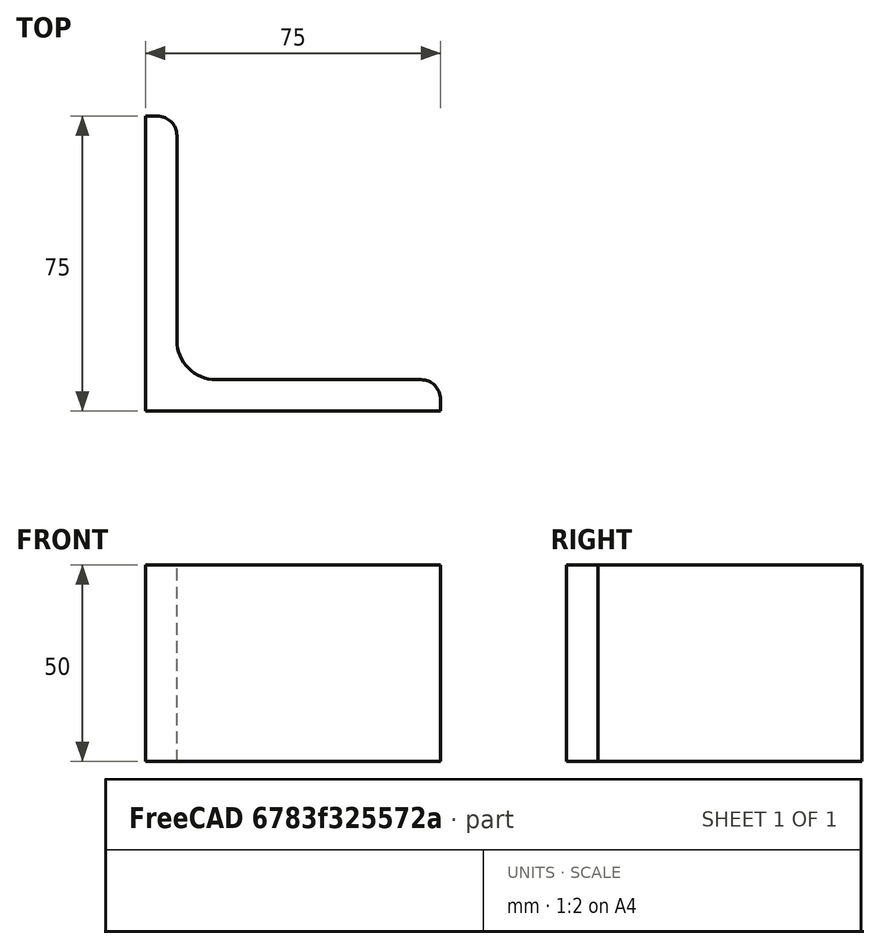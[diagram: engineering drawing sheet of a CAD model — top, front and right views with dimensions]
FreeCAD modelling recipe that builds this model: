
FCSTD DOCUMENT  (FreeCAD 0.15R4671 (Git))
Label: Angle Bar L75x75x8 EN10056 S235JR
License: All rights reserved
LicenseURL: http://en.wikipedia.org/wiki/All_rights_reserved
objects: Sketcher::SketchObject×1, Part::Extrusion×1
note: 2 computed .brp shape members not serialized (recipe doc carries the construction recipe); baked Part::Feature solids carry a one-line shape summary decoded from their .brp

FEATURE [Sketcher::SketchObject] Sketch
  sketch-geometry (9):
    g0: LineSegment StartX=0 StartY=0 StartZ=0 EndX=75 EndY=0 EndZ=0
    g1: LineSegment StartX=75 StartY=0 StartZ=0 EndX=75 EndY=3 EndZ=0
    g2: LineSegment StartX=70 StartY=8 StartZ=0 EndX=18 EndY=8 EndZ=0
    g3: LineSegment StartX=0 StartY=0 StartZ=0 EndX=0 EndY=75 EndZ=0
    g4: LineSegment StartX=0 StartY=75 StartZ=0 EndX=3 EndY=75 EndZ=0
    g5: LineSegment StartX=8 StartY=70 StartZ=0 EndX=8 EndY=18 EndZ=0
    g6: ArcOfCircle CenterX=18 CenterY=18 CenterZ=0 NormalX=0 NormalY=0 NormalZ=1 Radius=10 StartAngle=3.14159 EndAngle=4.71239
    g7: ArcOfCircle CenterX=3 CenterY=70 CenterZ=0 NormalX=0 NormalY=0 NormalZ=1 Radius=5 StartAngle=0 EndAngle=1.5708
    g8: ArcOfCircle CenterX=70 CenterY=3 CenterZ=0 NormalX=0 NormalY=0 NormalZ=1 Radius=5 StartAngle=0 EndAngle=1.5708
  constraints (23):
    c: Coincident(g0,g-1)
    c: Horizontal(g0)
    c: Coincident(g1,g0)
    c: Vertical(g1)
    c: Horizontal(g2)
    c: Coincident(g3,g-1)
    c: Vertical(g3)
    c: Coincident(g4,g3)
    c: Horizontal(g4)
    c: Vertical(g5)
    c: Tangent(g5,g6) = -1.5708
    c: Tangent(g2,g6) = 1.5708
    c: Tangent(g4,g7) = 1.5708
    c: Tangent(g5,g7) = 1.5708
    c: Tangent(g2,g8) = -1.5708
    c: Tangent(g1,g8) = -1.5708
    c: DistanceX(g0) = 75
    c: DistanceY(g3) = 75
    c: DistanceY(g0,g2) = 8
    c: DistanceX(g3,g5) = 8
    c: Radius(g6) = 10
    c: Radius(g8) = 5
    c: Radius(g7) = 5
FEATURE [Part::Extrusion] Extrude  label="Angle Bar L75x75x8 EN10056 S235JR"
  Base = -> Sketch
  Dir = (0,0,50)
  Solid = true
